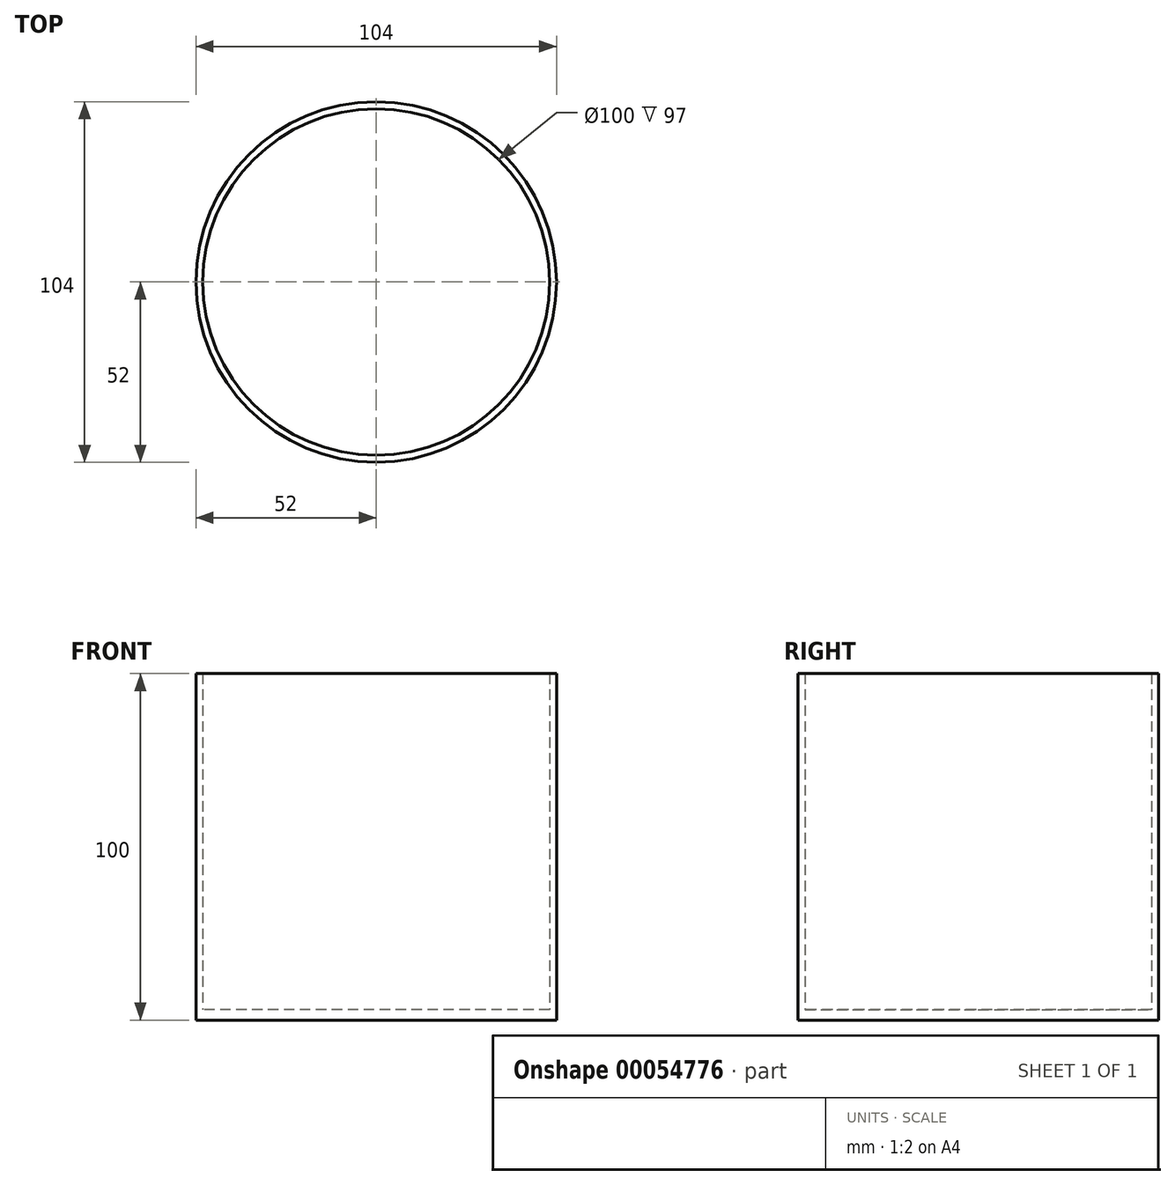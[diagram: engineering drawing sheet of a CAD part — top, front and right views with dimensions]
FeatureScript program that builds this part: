
annotation { "Feature Type Name" : "Feature", "Feature Type Description" : "" }
export const myFeature = defineFeature(function(context is Context, id is Id, definition is map)
    precondition{}
    {
        {
            var Q0;
            Q0=qCreatedBy(makeId("Top.planeOp"),FACE);
            var sketch = newSketch(context, id + "F0", { "sketchPlane" : qUnion([Q0])});
            skCircle(sketch, "E0", {"center": v(0, 0) * mm, "radius": 52 * mm});
            skCircle(sketch, "E1", {"center": v(0, 0) * mm, "radius": 50 * mm});
            skSolve(sketch);
        }
        {
            var Q0;
            Q0=makeQuery(id+"F0.imprint","IMPRINT",FACE,{"disambiguationData":[TD([[makeQuery(id+"F0.imprint","IMPRINT",EDGE,{"derivedFrom":sQuery(id+"F0.wireOp",EDGE,"E0")}),1.0]])]});
            extrude(context, id + "F1", {"entities" : qUnion([Q0]), "depth" : 100 * mm});
        }
        {
            var Q0;
            Q0=qCreatedBy(makeId("Top.planeOp"),FACE);
            var sketch = newSketch(context, id + "F2", { "sketchPlane" : qUnion([Q0])});
            skCircle(sketch, "E2.0", {"center": v(0, 0) * mm, "radius": 52 * mm});
            skSolve(sketch);
        }
        {
            var Q0;
            Q0=makeQuery(id+"F2.imprint","IMPRINT",FACE,{"disambiguationData":[TD([[makeQuery(id+"F2.imprint","IMPRINT",EDGE,{"derivedFrom":sQuery(id+"F2.wireOp",EDGE,"E2.0")}),1.0]])]});
            extrude(context, id + "F3", {"entities" : qUnion([Q0]), "operationType" : NewBodyOperationType.ADD, "depth" : 3 * mm});
        }
    });
